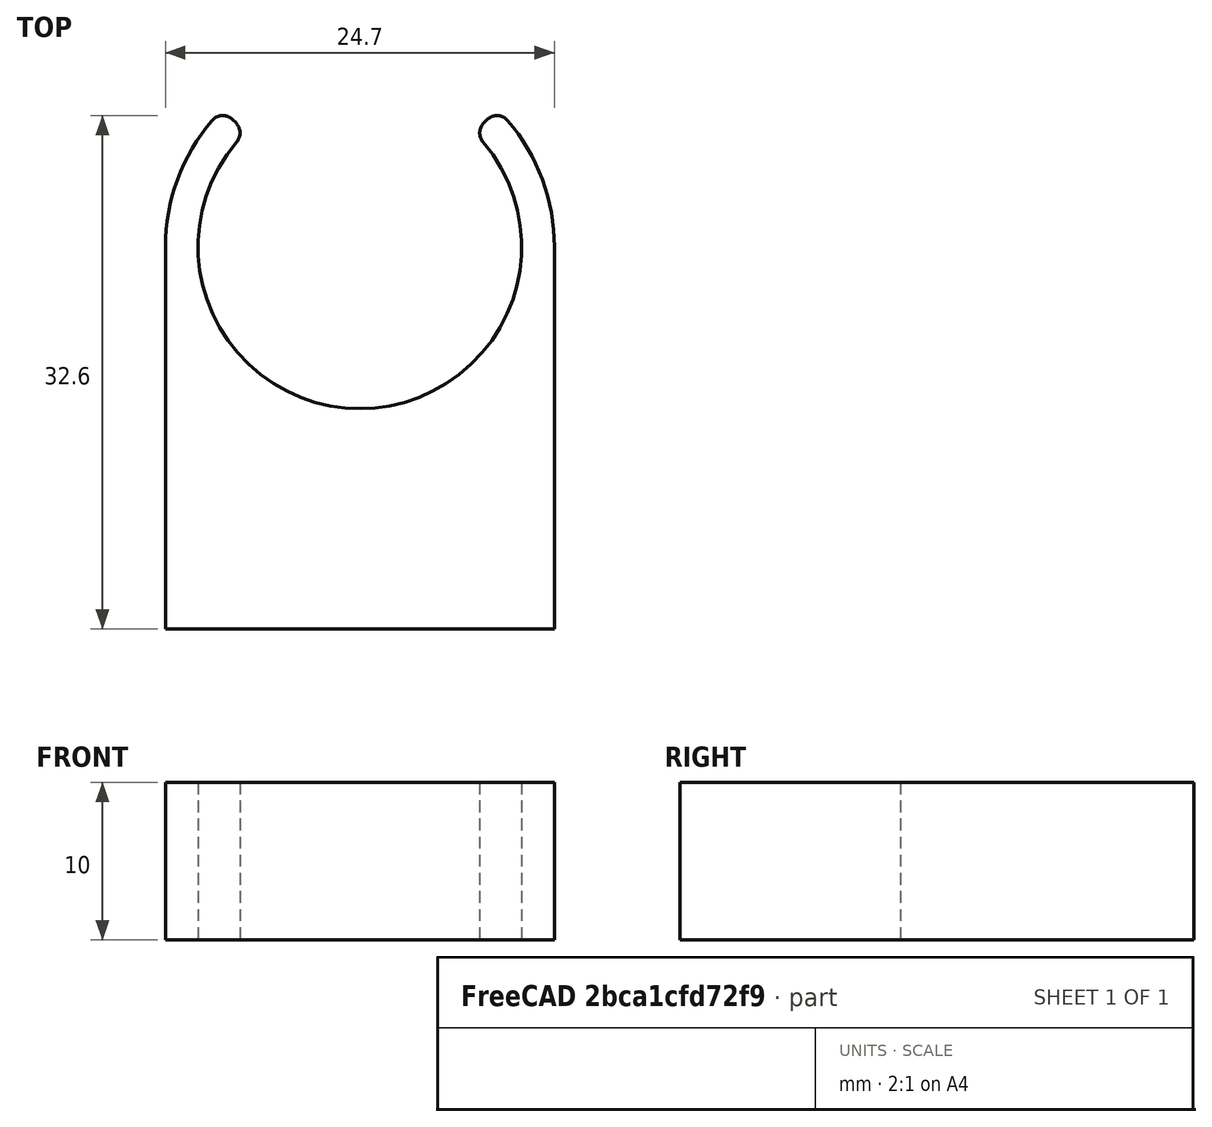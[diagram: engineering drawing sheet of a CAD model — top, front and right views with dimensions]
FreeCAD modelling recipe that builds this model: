
FCSTD DOCUMENT  (FreeCAD 0.19R24276 (Git))
Label: HalterFilter
License: All rights reserved
LicenseURL: http://en.wikipedia.org/wiki/All_rights_reserved
objects: Image::ImagePlane×1, Sketcher::SketchObject×1, PartDesign::Pad×1, PartDesign::Body×1
note: 4 computed .brp shape members not serialized (recipe doc carries the construction recipe); baked Part::Feature solids carry a one-line shape summary decoded from their .brp

FEATURE [Image::ImagePlane] ImagePlane
  Placement = pos=(0,0,-0.01) rot=(0,0,1;4.71239rad)
  XSize = 766
  YSize = 573
FEATURE [Sketcher::SketchObject] Sketch
  FullyConstrained = true
  MapMode = 5
  Support = -> [XY_Plane]
  expr: Constraints[2] = 180 - 45
  expr: Constraints[34] = 20.7 / 2 + 2
  sketch-geometry (15):
    g0: LineSegment StartX=-35.3553 StartY=35.3553 StartZ=0 EndX=0 EndY=0 EndZ=0
    g1: LineSegment StartX=0 StartY=0 StartZ=0 EndX=35.3553 EndY=35.3553 EndZ=0
    g2: ArcOfCircle CenterX=0 CenterY=0 CenterZ=0 NormalX=0 NormalY=0 NormalZ=1 AngleXU=0 Radius=10.275 StartAngle=2.43682 EndAngle=6.98796
    g3: LineSegment StartX=-8.07132 StartY=8.07132 StartZ=0 EndX=-7.87625 EndY=7.87625 EndZ=0
    g4: LineSegment StartX=7.87625 StartY=7.87625 StartZ=0 EndX=8.07132 EndY=8.07132 EndZ=0
    g5: ArcOfCircle CenterX=8.70772 CenterY=7.43493 CenterZ=0 NormalX=0 NormalY=0 NormalZ=1 AngleXU=0 Radius=0.9 StartAngle=0.706714 EndAngle=2.35619
    g6: ArcOfCircle CenterX=8.51265 CenterY=7.23985 CenterZ=0 NormalX=0 NormalY=0 NormalZ=1 AngleXU=0 Radius=0.9 StartAngle=2.35619 EndAngle=3.84637
    g7: ArcOfCircle CenterX=-8.70772 CenterY=7.43493 CenterZ=0 NormalX=0 NormalY=0 NormalZ=1 AngleXU=0 Radius=0.9 StartAngle=0.785398 EndAngle=2.43488
    g8: ArcOfCircle CenterX=-8.51265 CenterY=7.23985 CenterZ=0 NormalX=0 NormalY=0 NormalZ=1 AngleXU=0 Radius=0.9 StartAngle=5.57841 EndAngle=7.06858
    g9: LineSegment StartX=12.35 StartY=0 StartZ=0 EndX=12.35 EndY=-24.275 EndZ=0
    g10: LineSegment StartX=12.35 StartY=-24.275 StartZ=0 EndX=-12.35 EndY=-24.275 EndZ=0
    g11: LineSegment StartX=-12.35 StartY=-24.275 StartZ=0 EndX=-12.35 EndY=0 EndZ=0
    g12: GeomPoint X=0 Y=-10.275 Z=0
    g13: ArcOfCircle CenterX=0 CenterY=0 CenterZ=0 NormalX=0 NormalY=0 NormalZ=1 AngleXU=0 Radius=12.35 StartAngle=2.43488 EndAngle=3.14159
    g14: ArcOfCircle CenterX=0 CenterY=0 CenterZ=0 NormalX=0 NormalY=0 NormalZ=1 AngleXU=0 Radius=12.35 StartAngle=0 EndAngle=0.706714
  constraints (40):
    c: Coincident(g1,g0)
    c: Angle(g1,g0) = 1.5708
    c: Angle(g-2,g1) = 2.35619
    c: Equal(g1,g0)
    c: Coincident(g2,g-1)
    c: Coincident(g0,g2)
    c: Diameter(g2) = 20.55
    c: Tangent(g4,g5) = 1.5708
    c: Tangent(g2,g6) = 1.5708
    c: Tangent(g4,g6) = 1.5708
    c: Radius(g5) = 0.9
    c: Equal(g5,g6)
    c: PointOnObject(g4,g1)
    c: Tangent(g3,g7) = 1.5708
    c: Tangent(g3,g8) = 1.5708
    c: Tangent(g2,g8) = 1.5708
    c: Equal(g6,g8)
    c: Equal(g8,g7)
    c: PointOnObject(g3,g0)
    c: Distance(g1) = 50
    c: Coincident(g9,g10)
    c: Coincident(g10,g11)
    c: Horizontal(g10)
    c: Vertical(g9)
    c: Vertical(g11)
    c: PointOnObject(g12,g2)
    c: PointOnObject(g12,g-2)
    c: PointOnObject(g9,g-1)
    c: Distance(g12,g10) = 14
    c: PointOnObject(g11,g-1)
    c: Coincident(g13,g2)
    c: Coincident(g13,g11)
    c: Coincident(g14,g2)
    c: Coincident(g14,g9)
    c: Radius(g14) = 12.35
    c: Equal(g14,g13)
    c: Perpendicular(g13,g3)
    c: Perpendicular(g14,g4)
    c: Tangent(g13,g7) = -1.5708
    c: Tangent(g14,g5) = -1.5708
FEATURE [PartDesign::Pad] Pad
  Direction = (1,1,1)
  Length = 10
  Length2 = 100
  Profile = -> Sketch
  Type = 0
FEATURE [PartDesign::Body] Body
  Group = -> [Sketch,Pad]
  Origin = -> Origin
  Tip = -> Pad
